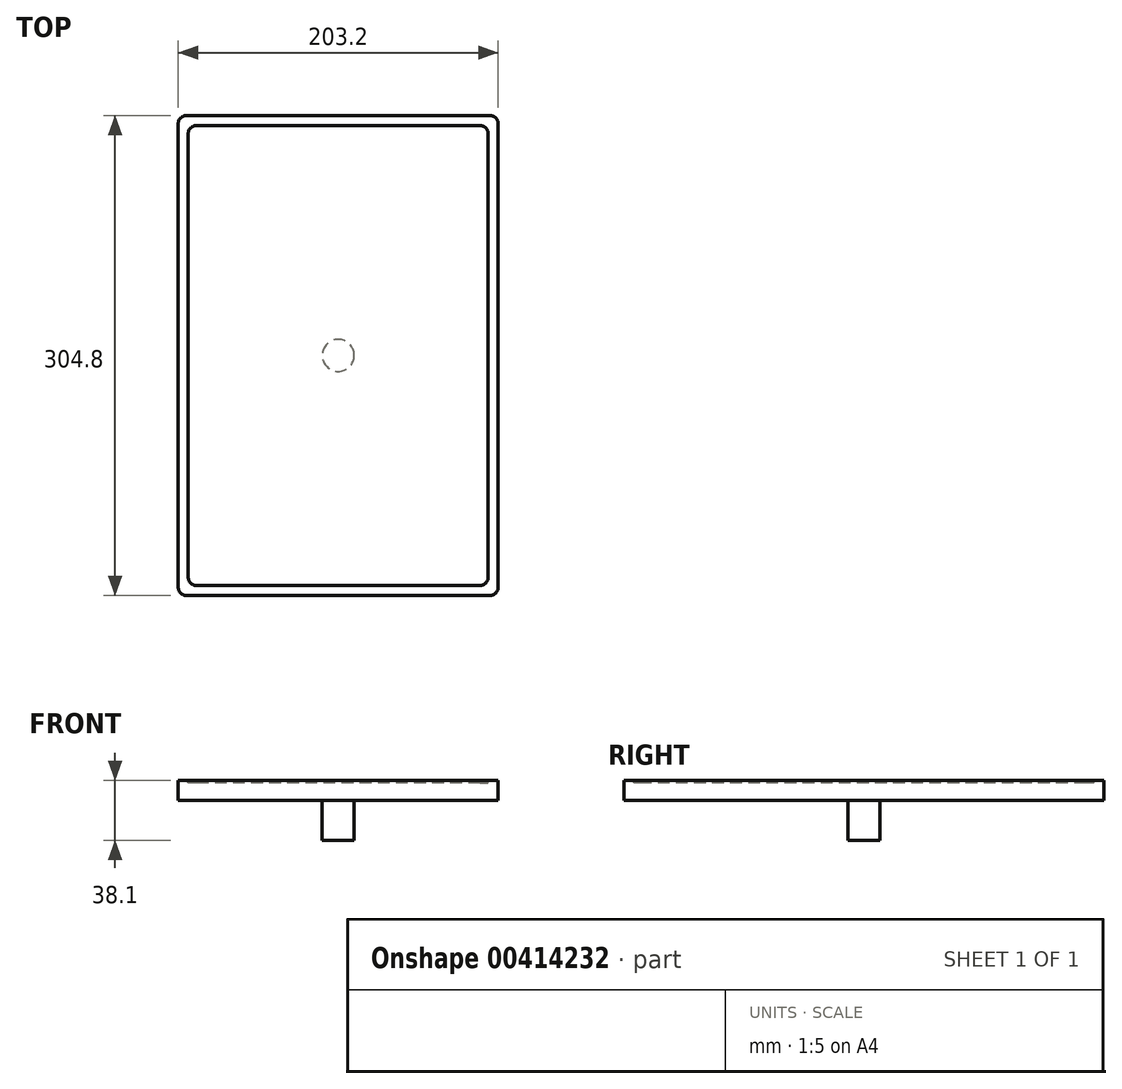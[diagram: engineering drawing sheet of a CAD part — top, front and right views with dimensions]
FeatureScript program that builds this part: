
annotation { "Feature Type Name" : "Feature", "Feature Type Description" : "" }
export const myFeature = defineFeature(function(context is Context, id is Id, definition is map)
    precondition{}
    {
        {
            var Q0;
            Q0=qCreatedBy(makeId("Top.planeOp"),FACE);
            var sketch = newSketch(context, id + "F0", { "sketchPlane" : qUnion([Q0])});
            skLineSegment(sketch, "E0.bottom", {"start": v(101.6, 152.4) * mm, "end": v(-101.6, 152.4) * mm});
            skLineSegment(sketch, "E0.top", {"start": v(101.6, -152.4) * mm, "end": v(-101.6, -152.4) * mm});
            skLineSegment(sketch, "E0.left", {"start": v(101.6, 152.4) * mm, "end": v(101.6, -152.4) * mm});
            skLineSegment(sketch, "E0.right", {"start": v(-101.6, 152.4) * mm, "end": v(-101.6, -152.4) * mm});
            skPoint(sketch, "E0.middle", {"position": v(0, 0) * mm});
            skSolve(sketch);
        }
        {
            var Q0;
            Q0=makeQuery(id+"F0.imprint","IMPRINT",FACE,{"disambiguationData":[TD([[makeQuery(id+"F0.imprint","IMPRINT",EDGE,{"derivedFrom":sQuery(id+"F0.wireOp",EDGE,"E0.bottom")}),1.0]])]});
            extrude(context, id + "F1", {"entities" : qUnion([Q0]), "depth" : 12.7 * mm});
        }
        {
            var Q0;
            Q0=makeQuery(id+"F1.opExtrude","SWEPT_EDGE",EDGE,{"disambiguationData":[OSD([sQuery(id+"F0.wireOp",EDGE,"E0.bottom"),sQuery(id+"F0.wireOp",EDGE,"E0.right")])]});
            var Q1;
            Q1=makeQuery(id+"F1.opExtrude","SWEPT_EDGE",EDGE,{"disambiguationData":[OSD([sQuery(id+"F0.wireOp",EDGE,"E0.top"),sQuery(id+"F0.wireOp",EDGE,"E0.right")])]});
            var Q2;
            Q2=makeQuery(id+"F1.opExtrude","SWEPT_EDGE",EDGE,{"disambiguationData":[OSD([sQuery(id+"F0.wireOp",EDGE,"E0.top"),sQuery(id+"F0.wireOp",EDGE,"E0.left")])]});
            var Q3;
            Q3=makeQuery(id+"F1.opExtrude","SWEPT_EDGE",EDGE,{"disambiguationData":[OSD([sQuery(id+"F0.wireOp",EDGE,"E0.bottom"),sQuery(id+"F0.wireOp",EDGE,"E0.left")])]});
            fillet(context, id + "F2", {"entities" : qUnion([Q0, Q1, Q2, Q3]), "radius" : 5.08 * mm, "tangentPropagation" : true, "allowEdgeOverflow" : false});
        }
        {
            var Q0;
            Q0=makeQuery(id+"F1.opExtrude","CAP_FACE",FACE,{"disambiguationData":[OSD([sQuery(id+"F0.wireOp",EDGE,"E0.bottom"),sQuery(id+"F0.wireOp",EDGE,"E0.top"),sQuery(id+"F0.wireOp",EDGE,"E0.left"),sQuery(id+"F0.wireOp",EDGE,"E0.right")])],"isStart":false});
            var sketch = newSketch(context, id + "F3", { "sketchPlane" : qUnion([Q0])});
            skLineSegment(sketch, "E1.bottom", {"start": v(95.25, 146.05) * mm, "end": v(-95.25, 146.05) * mm});
            skLineSegment(sketch, "E1.top", {"start": v(95.25, -146.05) * mm, "end": v(-95.25, -146.05) * mm});
            skLineSegment(sketch, "E1.left", {"start": v(95.25, 146.05) * mm, "end": v(95.25, -146.05) * mm});
            skLineSegment(sketch, "E1.right", {"start": v(-95.25, 146.05) * mm, "end": v(-95.25, -146.05) * mm});
            skPoint(sketch, "E1.middle", {"position": v(0, 0) * mm});
            skSolve(sketch);
        }
        {
            var Q0;
            Q0=makeQuery(id+"F3.imprint","IMPRINT",FACE,{"disambiguationData":[TD([[makeQuery(id+"F3.imprint","IMPRINT",EDGE,{"derivedFrom":sQuery(id+"F3.wireOp",EDGE,"E1.bottom")}),1.0]])]});
            extrude(context, id + "F4", {"entities" : qUnion([Q0]), "operationType" : NewBodyOperationType.REMOVE, "oppositeDirection" : true, "depth" : 3.17 * mm / 2});
        }
        {
            var Q0;
            Q0=makeQuery(id+"F4.boolean.opBoolean","COPY",EDGE,{"derivedFrom":makeQuery(id+"F4.opExtrude","SWEPT_EDGE",EDGE,{"disambiguationData":[OSD([sQuery(id+"F3.wireOp",EDGE,"E1.top"),sQuery(id+"F3.wireOp",EDGE,"E1.left")])]})});
            var Q1;
            Q1=makeQuery(id+"F4.boolean.opBoolean","COPY",EDGE,{"derivedFrom":makeQuery(id+"F4.opExtrude","SWEPT_EDGE",EDGE,{"disambiguationData":[OSD([sQuery(id+"F3.wireOp",EDGE,"E1.top"),sQuery(id+"F3.wireOp",EDGE,"E1.right")])]})});
            var Q2;
            Q2=makeQuery(id+"F4.boolean.opBoolean","COPY",EDGE,{"derivedFrom":makeQuery(id+"F4.opExtrude","SWEPT_EDGE",EDGE,{"disambiguationData":[OSD([sQuery(id+"F3.wireOp",EDGE,"E1.bottom"),sQuery(id+"F3.wireOp",EDGE,"E1.left")])]})});
            var Q3;
            Q3=makeQuery(id+"F4.boolean.opBoolean","COPY",EDGE,{"derivedFrom":makeQuery(id+"F4.opExtrude","SWEPT_EDGE",EDGE,{"disambiguationData":[OSD([sQuery(id+"F3.wireOp",EDGE,"E1.bottom"),sQuery(id+"F3.wireOp",EDGE,"E1.right")])]})});
            fillet(context, id + "F5", {"entities" : qUnion([Q0, Q1, Q2, Q3]), "radius" : 5.08 * mm, "tangentPropagation" : true, "allowEdgeOverflow" : false});
        }
        {
            var Q0;
            Q0=makeQuery(id+"F1.opExtrude","CAP_FACE",FACE,{"disambiguationData":[OSD([sQuery(id+"F0.wireOp",EDGE,"E0.bottom"),sQuery(id+"F0.wireOp",EDGE,"E0.top"),sQuery(id+"F0.wireOp",EDGE,"E0.left"),sQuery(id+"F0.wireOp",EDGE,"E0.right")])],"isStart":true});
            var sketch = newSketch(context, id + "F6", { "sketchPlane" : qUnion([Q0])});
            skCircle(sketch, "E2", {"center": v(0, 0) * mm, "radius": 10.16 * mm});
            skSolve(sketch);
        }
        {
            var Q0;
            Q0 = qSketchRegion(id + "F6", true);
            extrude(context, id + "F7", {"entities" : qUnion([Q0]), "operationType" : NewBodyOperationType.ADD, "depth" : 25.4 * mm});
        }
    });
